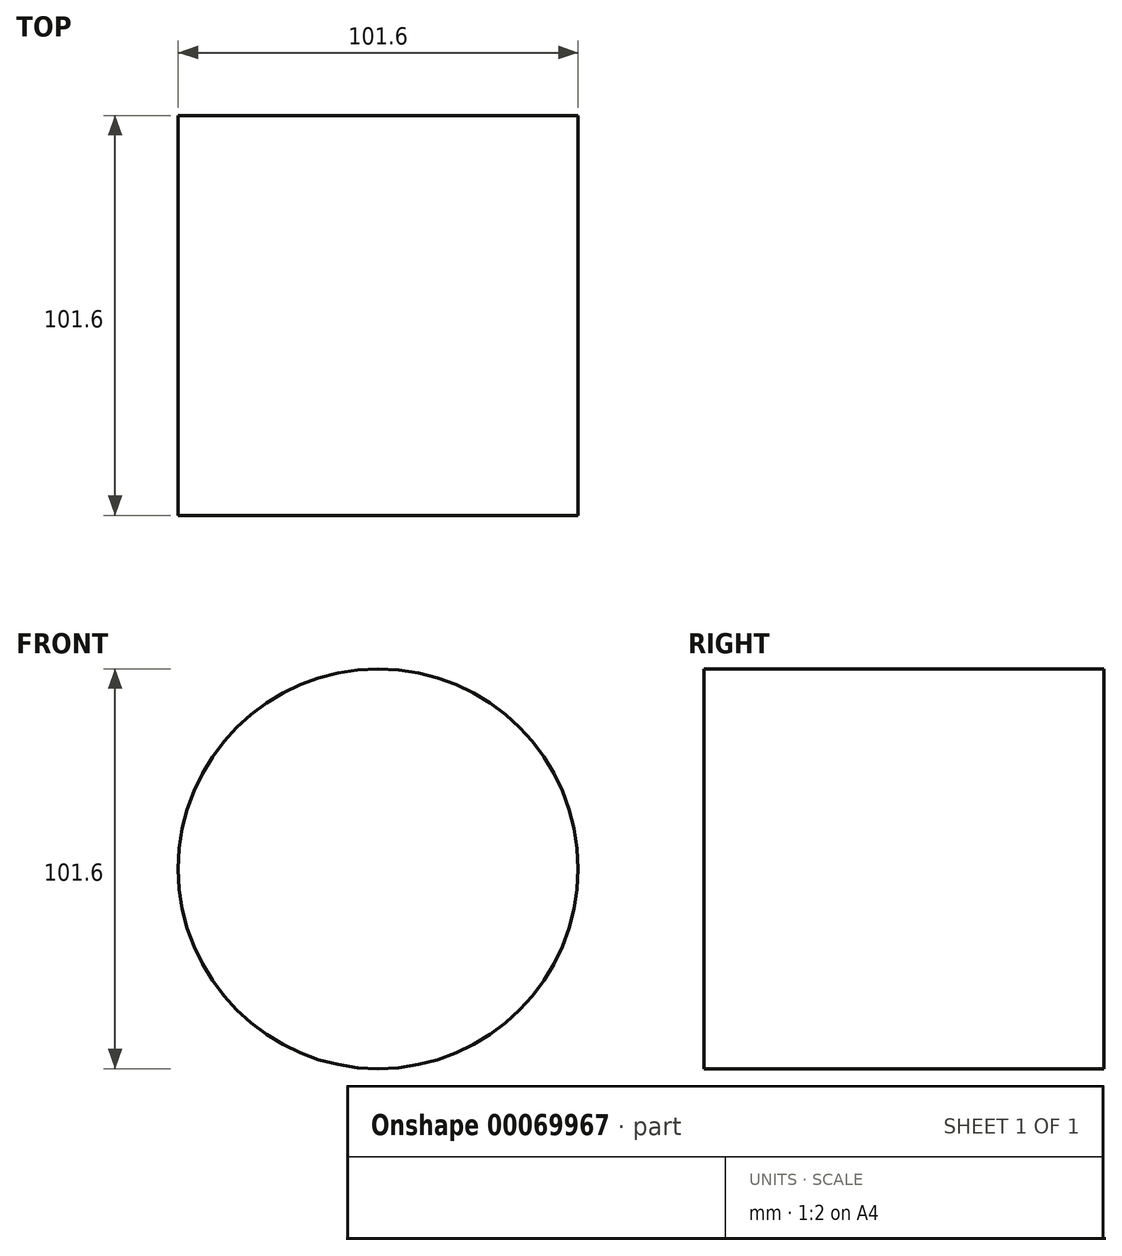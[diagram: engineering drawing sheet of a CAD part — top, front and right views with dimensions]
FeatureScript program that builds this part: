
annotation { "Feature Type Name" : "Feature", "Feature Type Description" : "" }
export const myFeature = defineFeature(function(context is Context, id is Id, definition is map)
    precondition{}
    {
        {
            var Q0;
            Q0=qCreatedBy(makeId("Front.planeOp"),FACE);
            var sketch = newSketch(context, id + "F0", { "sketchPlane" : qUnion([Q0])});
            skCircle(sketch, "E0", {"center": v(0, 0) * mm, "radius": 50.8 * mm});
            skSolve(sketch);
        }
        {
            var Q0;
            Q0=makeQuery(id+"F0.imprint","IMPRINT",FACE,{"disambiguationData":[TD([[makeQuery(id+"F0.imprint","IMPRINT",EDGE,{"derivedFrom":sQuery(id+"F0.wireOp",EDGE,"E0")}),1.0]])]});
            extrude(context, id + "F1", {"entities" : qUnion([Q0]), "depth" : 101.6 * mm});
        }
    });
